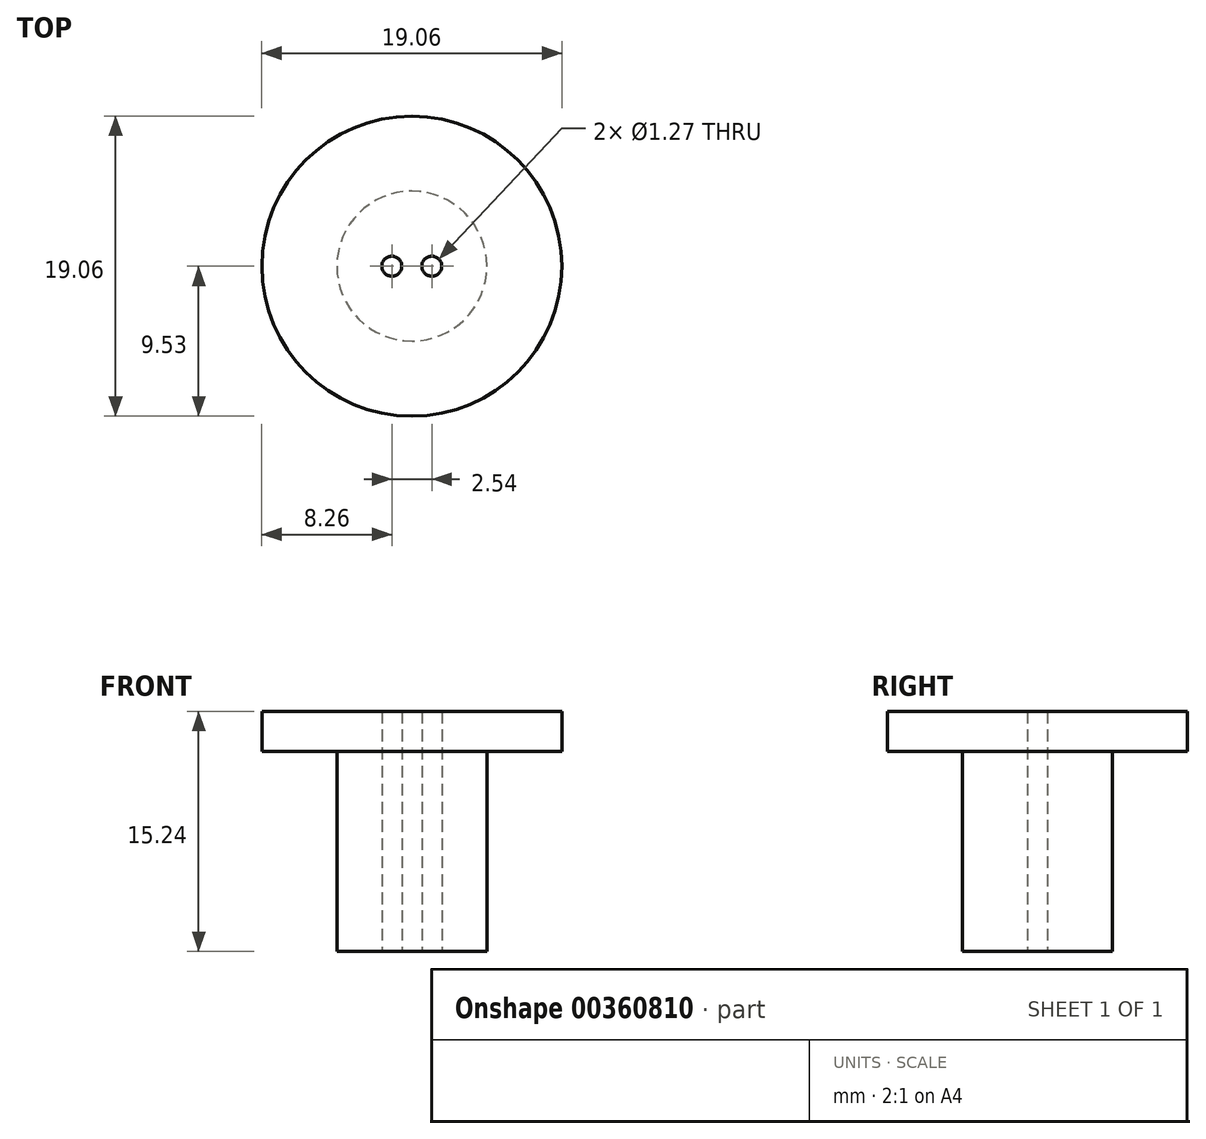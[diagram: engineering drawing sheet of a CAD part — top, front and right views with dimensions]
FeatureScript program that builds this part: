
annotation { "Feature Type Name" : "Feature", "Feature Type Description" : "" }
export const myFeature = defineFeature(function(context is Context, id is Id, definition is map)
    precondition{}
    {
        {
            var Q0;
            Q0=qCreatedBy(makeId("Top.planeOp"),FACE);
            var sketch = newSketch(context, id + "F0", { "sketchPlane" : qUnion([Q0])});
            skCircle(sketch, "E0", {"center": v(0, 0) * mm, "radius": 4.76 * mm});
            skCircle(sketch, "E1", {"center": v(-1.27, 0) * mm, "radius": 0.64 * mm});
            skCircle(sketch, "E2", {"center": v(1.27, 0) * mm, "radius": 0.64 * mm});
            skSolve(sketch);
        }
        {
            var Q0;
            Q0=makeQuery(id+"F0.imprint","IMPRINT",FACE,{"disambiguationData":[TD([[makeQuery(id+"F0.imprint","IMPRINT",EDGE,{"derivedFrom":sQuery(id+"F0.wireOp",EDGE,"E0")}),1.0]])]});
            extrude(context, id + "F1", {"entities" : qUnion([Q0]), "depth" : 12.7 * mm});
        }
        {
            var Q0;
            Q0=makeQuery(id+"F1.opExtrude","CAP_FACE",FACE,{"disambiguationData":[OSD([sQuery(id+"F0.wireOp",EDGE,"E0"),sQuery(id+"F0.wireOp",EDGE,"E1"),sQuery(id+"F0.wireOp",EDGE,"E2")])],"isStart":false});
            var sketch = newSketch(context, id + "F2", { "sketchPlane" : qUnion([Q0])});
            skCircle(sketch, "E3", {"center": v(0, 0) * mm, "radius": 9.53 * mm});
            skCircle(sketch, "E4", {"center": v(-1.27, 0) * mm, "radius": 0.64 * mm});
            skCircle(sketch, "E5", {"center": v(1.27, 0) * mm, "radius": 0.64 * mm});
            skSolve(sketch);
        }
        {
            var Q0;
            Q0=makeQuery(id+"F2.imprint","IMPRINT",FACE,{"disambiguationData":[TD([[makeQuery(id+"F2.imprint","IMPRINT",EDGE,{"derivedFrom":sQuery(id+"F2.wireOp",EDGE,"E3")}),1.0]])]});
            var Q1;
            Q1=makeQuery(id+"F2.imprint","IMPRINT",FACE,{"disambiguationData":[TD([[makeQuery(id+"F2.imprint","IMPRINT",EDGE,{"derivedFrom":sQuery(id+"F2.wireOp",EDGE,"E4")}),-1.0]])]});
            extrude(context, id + "F3", {"entities" : qUnion([Q0, Q1]), "operationType" : NewBodyOperationType.ADD, "depth" : 2.54 * mm});
        }
    });
